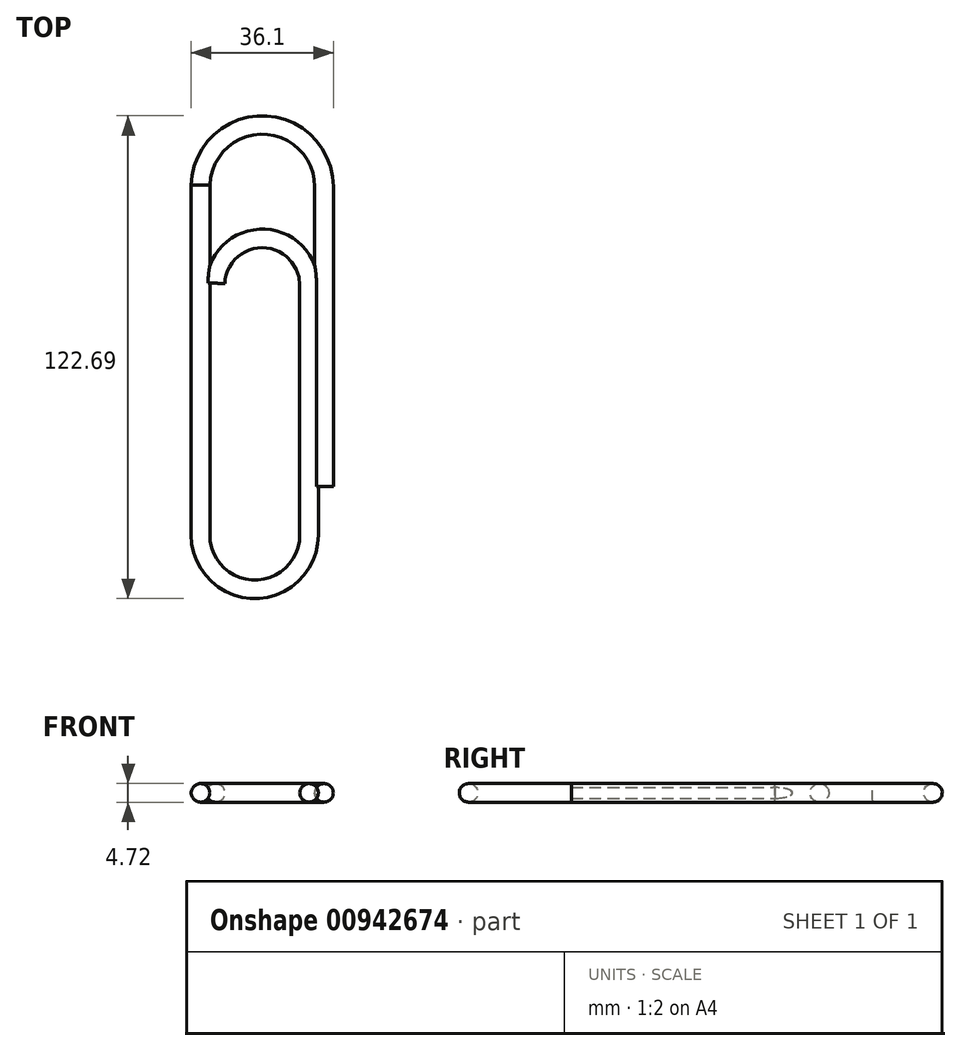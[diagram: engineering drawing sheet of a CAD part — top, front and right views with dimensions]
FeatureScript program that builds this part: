
annotation { "Feature Type Name" : "Feature", "Feature Type Description" : "" }
export const myFeature = defineFeature(function(context is Context, id is Id, definition is map)
    precondition{}
    {
        {
            var Q0;
            Q0=qCreatedBy(makeId("Top.planeOp"),FACE);
            var sketch = newSketch(context, id + "F0", { "sketchPlane" : qUnion([Q0])});
            skLineSegment(sketch, "E0", {"start": v(58.46, 0) * mm, "end": v(58.46, 76.2) * mm});
            skArc(sketch, "E1", {"start": v(58.46, 76.2) * mm, "mid": v(43.42, 91.44) * mm, "end": v(27.98, 76.6) * mm});
            skLineSegment(sketch, "E2", {"start": v(27.98, 76.6) * mm, "end": v(27.98, -12.3) * mm});
            skArc(sketch, "E3", {"start": v(27.98, -12.3) * mm, "mid": v(41.32, -25.63) * mm, "end": v(54.65, -12.3) * mm});
            skLineSegment(sketch, "E4", {"start": v(54.65, -12.3) * mm, "end": v(54.65, 51.2) * mm});
            skArc(sketch, "E5", {"start": v(54.65, 51.2) * mm, "mid": v(43.46, 62.63) * mm, "end": v(31.8, 51.68) * mm});
            skLineSegment(sketch, "E6", {"start": v(31.8, 51.68) * mm, "end": v(31.8, -11.82) * mm});
            skSolve(sketch);
        }
        {
            var Q0;
            Q0=qCreatedBy(makeId("Front.planeOp"),FACE);
            var Q1;
            Q1=sQuery(id+"F0.wireOp",VERTEX,"E0.start");
            cPlane(context, id + "F1", {"entities" : qUnion([Q0, Q1]), "cplaneType" : CPlaneType.PLANE_POINT, "offset" : 25.4 * mm, "width" : 152.4 * mm, "height" : 152.4 * mm});
        }
        {
            var Q0;
            Q0=qCreatedBy(id+"F1.planeOp",FACE);
            var sketch = newSketch(context, id + "F2", { "sketchPlane" : qUnion([Q0])});
            skCircle(sketch, "E7", {"center": v(58.9, 0) * mm, "radius": 2.36 * mm});
            skSolve(sketch);
        }
        {
            var Q0;
            Q0=makeQuery(id+"F2.imprint","IMPRINT",FACE,{"disambiguationData":[TD([[makeQuery(id+"F2.imprint","IMPRINT",EDGE,{"derivedFrom":sQuery(id+"F2.wireOp",EDGE,"E7")}),1.0]])]});
            var Q1;
            Q1=sQuery(id+"F0.wireOp",EDGE,"E0");
            var Q2;
            Q2=sQuery(id+"F0.wireOp",EDGE,"E1");
            var Q3;
            Q3=sQuery(id+"F0.wireOp",EDGE,"E2");
            var Q4;
            Q4=sQuery(id+"F0.wireOp",EDGE,"E3");
            var Q5;
            Q5=sQuery(id+"F0.wireOp",EDGE,"E4");
            var Q6;
            Q6=sQuery(id+"F0.wireOp",EDGE,"E5");
            sweep(context, id + "F3", {"profiles" : qUnion([Q0]), "path" : qUnion([Q1, Q2, Q3, Q4, Q5, Q6])});
        }
    });
